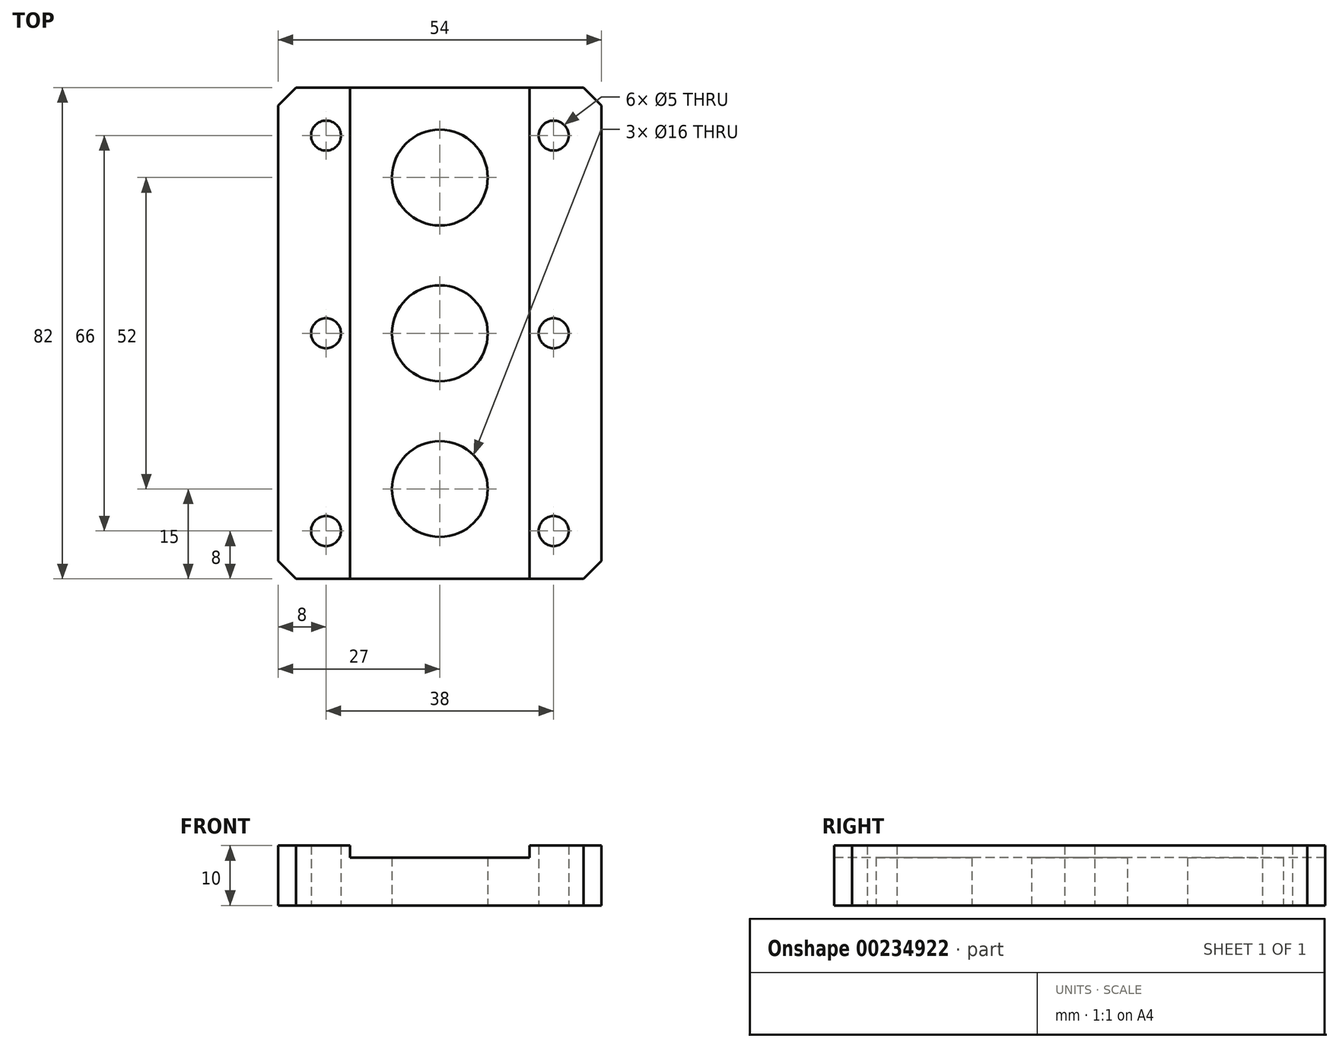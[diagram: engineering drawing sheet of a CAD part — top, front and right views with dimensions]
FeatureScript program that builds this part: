
annotation { "Feature Type Name" : "Feature", "Feature Type Description" : "" }
export const myFeature = defineFeature(function(context is Context, id is Id, definition is map)
    precondition{}
    {
        {
            var Q0;
            Q0=qCreatedBy(makeId("Top.planeOp"),FACE);
            var sketch = newSketch(context, id + "F0", { "sketchPlane" : qUnion([Q0])});
            skLineSegment(sketch, "E0.bottom", {"start": v(27, 41) * mm, "end": v(-27, 41) * mm});
            skLineSegment(sketch, "E0.top", {"start": v(27, -41) * mm, "end": v(-27, -41) * mm});
            skLineSegment(sketch, "E0.left", {"start": v(27, 41) * mm, "end": v(27, -41) * mm});
            skLineSegment(sketch, "E0.right", {"start": v(-27, 41) * mm, "end": v(-27, -41) * mm});
            skPoint(sketch, "E0.middle", {"position": v(0, 0) * mm});
            skLineSegment(sketch, "E1", {"start": v(0, 41) * mm, "end": v(0, -41) * mm, "construction": true});
            skLineSegment(sketch, "E2", {"start": v(-27, 0) * mm, "end": v(27, 0) * mm, "construction": true});
            skCircle(sketch, "E3", {"center": v(0, -26) * mm, "radius": 8 * mm});
            skCircle(sketch, "E4", {"center": v(0, 26) * mm, "radius": 8 * mm});
            skLineSegment(sketch, "E5", {"start": v(-19, 41) * mm, "end": v(-19, -41) * mm, "construction": true});
            skCircle(sketch, "E6", {"center": v(-19, 0) * mm, "radius": 2.5 * mm});
            skCircle(sketch, "E7", {"center": v(-19, 33) * mm, "radius": 2.5 * mm});
            skCircle(sketch, "E8", {"center": v(-19, -33) * mm, "radius": 2.5 * mm});
            skCircle(sketch, "E9.MirrorC", {"center": v(19, -33) * mm, "radius": 2.5 * mm});
            skCircle(sketch, "E10.MirrorC", {"center": v(19, 33) * mm, "radius": 2.5 * mm});
            skCircle(sketch, "E11.MirrorC", {"center": v(19, 0) * mm, "radius": 2.5 * mm});
            skSolve(sketch);
        }
        {
            var Q0;
            Q0=qSketchRegion(id+"F0",true);
            extrude(context, id + "F1", {"entities" : qUnion([Q0]), "depth" : 10 * mm});
        }
        {
            var Q0;
            Q0=makeQuery(id+"F1.opExtrude","SWEPT_EDGE",EDGE,{"disambiguationData":[OSD([sQuery(id+"F0.wireOp",EDGE,"E0.top"),sQuery(id+"F0.wireOp",EDGE,"E0.left")])]});
            var Q1;
            Q1=makeQuery(id+"F1.opExtrude","SWEPT_EDGE",EDGE,{"disambiguationData":[OSD([sQuery(id+"F0.wireOp",EDGE,"E0.top"),sQuery(id+"F0.wireOp",EDGE,"E0.right")])]});
            var Q2;
            Q2=makeQuery(id+"F1.opExtrude","SWEPT_EDGE",EDGE,{"disambiguationData":[OSD([sQuery(id+"F0.wireOp",EDGE,"E0.bottom"),sQuery(id+"F0.wireOp",EDGE,"E0.left")])]});
            var Q3;
            Q3=makeQuery(id+"F1.opExtrude","SWEPT_EDGE",EDGE,{"disambiguationData":[OSD([sQuery(id+"F0.wireOp",EDGE,"E0.bottom"),sQuery(id+"F0.wireOp",EDGE,"E0.right")])]});
            chamfer(context, id + "F2", {"entities" : qUnion([Q0, Q1, Q2, Q3]), "width" : 3 * mm, "tangentPropagation" : true});
        }
        {
            var Q0;
            Q0=makeQuery(id+"F1.opExtrude","CAP_FACE",FACE,{"disambiguationData":[OSD([sQuery(id+"F0.wireOp",EDGE,"E0.bottom"),sQuery(id+"F0.wireOp",EDGE,"E0.top"),sQuery(id+"F0.wireOp",EDGE,"E0.left"),sQuery(id+"F0.wireOp",EDGE,"E0.right"),sQuery(id+"F0.wireOp",EDGE,"E3"),sQuery(id+"F0.wireOp",EDGE,"E4"),sQuery(id+"F0.wireOp",EDGE,"E8"),sQuery(id+"F0.wireOp",EDGE,"E6"),sQuery(id+"F0.wireOp",EDGE,"E7"),sQuery(id+"F0.wireOp",EDGE,"E9.MirrorC"),sQuery(id+"F0.wireOp",EDGE,"E10.MirrorC"),sQuery(id+"F0.wireOp",EDGE,"E11.MirrorC")])],"isStart":false});
            var sketch = newSketch(context, id + "F3", { "sketchPlane" : qUnion([Q0])});
            skLineSegment(sketch, "E12", {"start": v(0, 41) * mm, "end": v(0, -41) * mm, "construction": true});
            skLineSegment(sketch, "E13", {"start": v(-15, 41) * mm, "end": v(-15, -41) * mm});
            skLineSegment(sketch, "E14", {"start": v(15, 41) * mm, "end": v(15, -41) * mm});
            skLineSegment(sketch, "E15", {"start": v(-15, 41) * mm, "end": v(15, 41) * mm});
            skLineSegment(sketch, "E16", {"start": v(-15, -41) * mm, "end": v(15, -41) * mm});
            skSolve(sketch);
        }
        {
            var Q0;
            Q0=qSketchRegion(id+"F3",true);
            extrude(context, id + "F4", {"entities" : qUnion([Q0]), "operationType" : NewBodyOperationType.REMOVE, "oppositeDirection" : true, "depth" : 2 * mm});
        }
        {
            var Q0;
            Q0=makeQuery(id+"F4.boolean.opBoolean","COPY",FACE,{"derivedFrom":makeQuery(id+"F4.opExtrude","CAP_FACE",FACE,{"disambiguationData":[OSD([sQuery(id+"F3.wireOp",EDGE,"E13"),sQuery(id+"F3.wireOp",EDGE,"E14"),sQuery(id+"F3.wireOp",EDGE,"E15"),sQuery(id+"F3.wireOp",EDGE,"E16")])],"isStart":false})});
            var sketch = newSketch(context, id + "F5", { "sketchPlane" : qUnion([Q0])});
            skCircle(sketch, "E17", {"center": v(0, 0) * mm, "radius": 8 * mm});
            skSolve(sketch);
        }
        {
            var Q0;
            Q0 = qSketchRegion(id + "F5", true);
            extrude(context, id + "F6", {"entities" : qUnion([Q0]), "operationType" : NewBodyOperationType.REMOVE, "oppositeDirection" : true, "depth" : 25 * mm, "offsetDistance" : 25 * mm});
        }
    });
